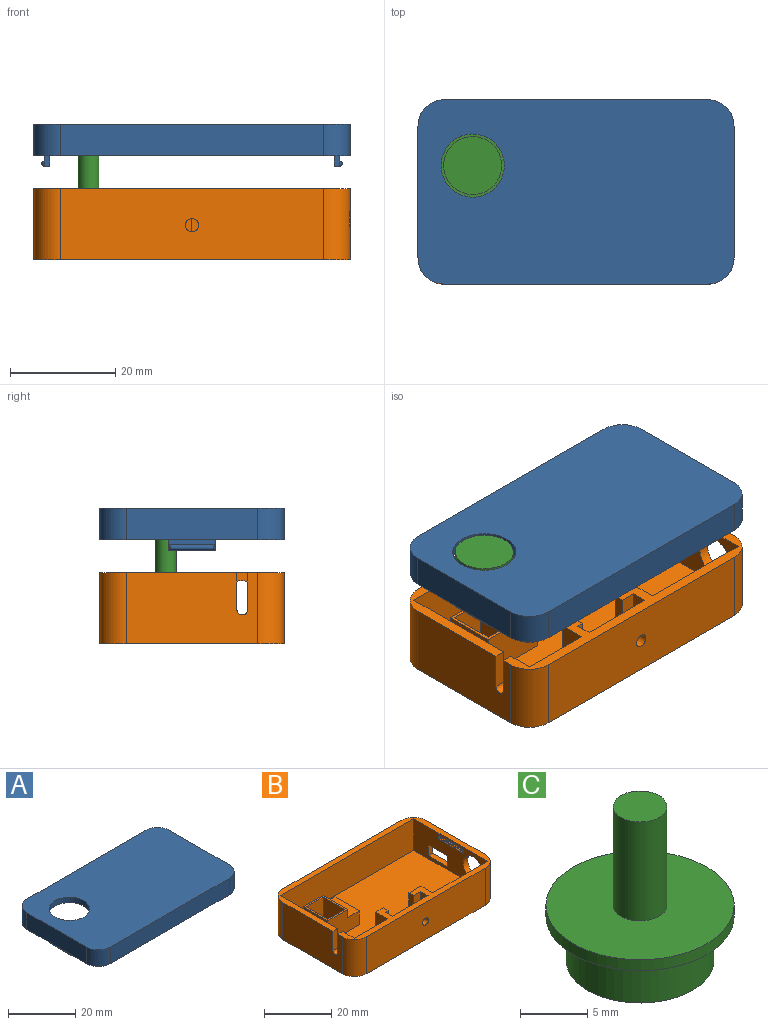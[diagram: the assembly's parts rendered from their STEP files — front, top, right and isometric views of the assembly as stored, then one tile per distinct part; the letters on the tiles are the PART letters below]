
ASSEMBLY  parts=3 mates=2
PART A: 30 faces, bbox 60x35x8 mm
  f0: plane 60x35mm, normal (0,0,-1), area 386.5mm2, adj f1,f2,f3,f4,f6,f7,f8,f9
  f1: plane 50x6mm, normal (0,1,0), area 300mm2, adj f0,f5,f28,f29
  f2: plane 25x6mm, normal (-1,0,0), area 150mm2, adj f0,f5,f26,f29
  f3: plane 50x6mm, normal (0,-1,0), area 300mm2, adj f0,f5,f26,f27
  f4: plane 25x6mm, normal (1,0,0), area 150mm2, adj f0,f5,f27,f28
  f5: plane 60x35mm, normal (0,0,1), area 1965.4mm2, adj f1,f2,f3,f4,f11,f26,f27,f28
  f6: plane 54x4mm, normal (0,-1,0), area 216mm2, adj f0,f7,f9,f10
  f7: plane 31x6mm, normal (1,0,0), area 142mm2, adj f0,f6,f8,f10,f12,f14,f15
  f8: plane 54x4mm, normal (0,1,0), area 216mm2, adj f0,f7,f9,f10
  f9: plane 31x6mm, normal (-1,0,0), area 142mm2, adj f0,f6,f8,f10,f17,f18,f19
  f10: plane 54x31mm, normal (0,0,-1), area 1560.9mm2, adj f6,f7,f8,f9,f11
  f11: cylinder r=6mm len=12mm, axis (0,0,-1), area 75.4mm2, adj f5,f10
  f12: plane 2x1mm, normal (0,1,0), area 2mm2, adj f0,f7,f13,f15,f22
  f13: plane 9x1mm, normal (-1,0,0), area 9mm2, adj f0,f12,f14,f21
  f14: plane 2x1mm, normal (0,-1,0), area 2mm2, adj f0,f7,f13,f15,f20
  f15: plane 9x1mm, normal (0,0,-1), area 9mm2, adj f7,f12,f14,f21
  f16: plane 9x1mm, normal (1,0,0), area 9mm2, adj f0,f17,f18,f23
  f17: plane 2x1mm, normal (0,1,0), area 2mm2, adj f0,f9,f16,f19,f24
  f18: plane 2x1mm, normal (0,-1,0), area 2mm2, adj f0,f9,f16,f19,f25
  f19: plane 9x1mm, normal (0,0,-1), area 9mm2, adj f9,f17,f18,f23
  f20: cylinder r=0.5mm len=1mm, axis (0,0,-1), area 0.5mm2, adj f14,f21
  f21: cylinder r=0.5mm len=9mm, axis (0,1,0), area 13.6mm2, adj f13,f15,f20,f22
  f22: cylinder r=0.5mm len=1mm, axis (0,0,1), area 0.5mm2, adj f12,f21
  f23: cylinder r=0.5mm len=9mm, axis (0,1,0), area 13.6mm2, adj f16,f19,f24,f25
  f24: cylinder r=0.5mm len=1mm, axis (0,0,1), area 0.5mm2, adj f17,f23
  f25: cylinder r=0.5mm len=1mm, axis (0,0,-1), area 0.5mm2, adj f18,f23
  f26: cylinder r=5mm len=6mm, axis (0,0,-1), area 47.1mm2, adj f0,f2,f3,f5
  f27: cylinder r=5mm len=6mm, axis (0,0,1), area 47.1mm2, adj f0,f3,f4,f5
  f28: cylinder r=5mm len=6mm, axis (0,0,-1), area 47.1mm2, adj f0,f1,f4,f5
  f29: cylinder r=5mm len=6mm, axis (0,0,1), area 47.1mm2, adj f0,f1,f2,f5
PART B: 74 faces, bbox 60x35x13.5 mm
  f0: plane 31x11.5mm, normal (1,0,0), area 324mm2, adj f2,f3,f7,f11,f54,f55,f56,f62
  f1: plane 25x13.5mm, normal (-1,0,0), area 321.9mm2, adj f7,f10,f54,f55,f56,f70,f71
  f2: plane 56x31mm, normal (0,0,1), area 1573mm2, adj f0,f3,f4,f5,f11,f12,f31,f32
  f3: plane 14x11.5mm, normal (0,1,0), area 161mm2, adj f0,f2,f7,f40
  f4: plane 15x11.5mm, normal (0,1,0), area 167.6mm2, adj f2,f7,f34,f36,f51
  f5: plane 31x11.5mm, normal (-1,0,0), area 250.8mm2, adj f2,f7,f11,f12,f13,f14,f15,f16
  f6: plane 25x13.5mm, normal (1,0,0), area 253.8mm2, adj f7,f10,f13,f14,f15,f16,f17,f72
  f7: plane 60x35mm, normal (0,0,1), area 366.9mm2, adj f0,f1,f3,f4,f5,f6,f8,f9
  f8: plane 50x13.5mm, normal (0,1,0), area 675mm2, adj f7,f10,f70,f73
  f9: plane 50x13.5mm, normal (0,-1,0), area 670.1mm2, adj f7,f10,f51,f71,f72
  f10: plane 60x35mm, normal (0,0,-1), area 2078.5mm2, adj f1,f6,f8,f9,f70,f71,f72,f73
  f11: plane 56x11.5mm, normal (0,-1,0), area 644mm2, adj f0,f2,f5,f7
  f12: plane 23x11.5mm, normal (0,1,0), area 264.5mm2, adj f2,f5,f7,f31
  f13: cylinder r=4.25mm len=8.5mm, axis (-1,0,0), area 52.9mm2, adj f5,f6,f72
  f14: plane 8x2mm, normal (0,0,-1), area 16mm2, adj f5,f6,f15,f17
  f15: plane 4x2mm, normal (0,-1,0), area 8mm2, adj f5,f6,f14,f16
  f16: plane 8x2mm, normal (0,0,1), area 16mm2, adj f5,f6,f15,f17
  f17: plane 4x2mm, normal (0,1,0), area 8mm2, adj f5,f6,f14,f16
  f18: plane 1x0.4mm, normal (0,-1,0), area 0.4mm2, adj f19,f21,f23,f27
  f19: plane 10x0.4mm, normal (0,0,1), area 4mm2, adj f18,f20,f24,f28
  f20: plane 1x0.4mm, normal (0,1,0), area 0.4mm2, adj f19,f21,f26,f30
  f21: plane 10x0.4mm, normal (0,0,-1), area 4mm2, adj f18,f20,f25,f29
  f22: plane 9.4x0.4mm, normal (-1,0,0), area 3.8mm2, adj f27,f28,f29,f30
  f23: cylinder r=0.3mm len=1.6mm, axis (0,0,-1), area 0.6mm2, adj f5,f18,f24,f25
  f24: cylinder r=0.3mm len=10.6mm, axis (0,-1,0), area 4.8mm2, adj f5,f19,f23,f26
  f25: cylinder r=0.3mm len=10.6mm, axis (0,1,0), area 4.8mm2, adj f5,f21,f23,f26
  f26: cylinder r=0.3mm len=1.6mm, axis (0,0,1), area 0.6mm2, adj f5,f20,f24,f25
  f27: cylinder r=0.3mm len=1mm, axis (0,0,-1), area 0.4mm2, adj f18,f22,f28,f29
  f28: cylinder r=0.3mm len=10mm, axis (0,-1,0), area 4.6mm2, adj f19,f22,f27,f30
  f29: cylinder r=0.3mm len=10mm, axis (0,1,0), area 4.6mm2, adj f21,f22,f27,f30
  f30: cylinder r=0.3mm len=1mm, axis (0,0,1), area 0.4mm2, adj f20,f22,f28,f29
  f31: plane 11.5x5mm, normal (1,0,0), area 57.5mm2, adj f2,f7,f12,f32
  f32: plane 11.5x5mm, normal (0,1,0), area 57.5mm2, adj f2,f7,f31,f33
  f33: plane 11.5x2mm, normal (-1,0,0), area 23mm2, adj f2,f7,f32,f35
  f34: plane 11.5x3mm, normal (-1,0,0), area 34.5mm2, adj f2,f4,f7,f35
  f35: plane 11.5x3mm, normal (0,-1,0), area 34.5mm2, adj f2,f7,f33,f34
  f36: plane 11.5x3mm, normal (1,0,0), area 34.5mm2, adj f2,f4,f7,f37
  f37: plane 11.5x1.2mm, normal (0,-1,0), area 13.8mm2, adj f2,f7,f36,f38
  f38: plane 11.5x2mm, normal (1,0,0), area 23mm2, adj f2,f7,f37,f39
  f39: plane 11.5x3.2mm, normal (0,1,0), area 36.8mm2, adj f2,f7,f38,f40
  f40: plane 11.5x5mm, normal (-1,0,0), area 57.5mm2, adj f2,f3,f7,f39
  f41: plane 10.2x8mm, normal (-1,0,0), area 81.6mm2, adj f2,f42,f48,f49
  f42: plane 13.2x8mm, normal (0,-1,0), area 90.6mm2, adj f2,f41,f43,f49,f52,f53
  f43: plane 10.2x3mm, normal (1,0,0), area 30.6mm2, adj f42,f48,f49,f52
  f44: plane 9x8mm, normal (-1,0,0), area 72mm2, adj f45,f47,f49,f50
  f45: plane 8x7mm, normal (0,1,0), area 56mm2, adj f44,f46,f49,f50
  f46: plane 9x8mm, normal (1,0,0), area 72mm2, adj f45,f47,f49,f50
  f47: plane 8x7mm, normal (0,-1,0), area 56mm2, adj f44,f46,f49,f50
  f48: plane 13.2x8mm, normal (0,1,0), area 90.6mm2, adj f2,f41,f43,f49,f52,f53
  f49: plane 10.2x8.2mm, normal (0,0,1), area 20.6mm2, adj f41,f42,f43,f44,f45,f46,f47,f48
  f50: plane 9x7mm, normal (0,0,1), area 63mm2, adj f44,f45,f46,f47
  f51: cylinder r=1.25mm len=2.5mm, axis (0,1,0), area 15.7mm2, adj f4,f9
  f52: plane 10.2x5mm, normal (0,0,1), area 51mm2, adj f42,f43,f48,f53
  f53: plane 10.2x5mm, normal (1,0,0), area 51mm2, adj f2,f42,f48,f52
  f54: plane 7x2mm, normal (0,1,0), area 14mm2, adj f0,f1,f7,f55
  f55: cylinder r=1mm len=2mm, axis (1,0,0), area 6.3mm2, adj f0,f1,f54,f56
  f56: plane 7x2mm, normal (0,-1,0), area 14mm2, adj f0,f1,f7,f55
  f57: plane 10x0.4mm, normal (0,0,1), area 4mm2, adj f58,f60,f62,f66
  f58: plane 1x0.4mm, normal (0,-1,0), area 0.4mm2, adj f57,f59,f63,f67
  f59: plane 10x0.4mm, normal (0,0,-1), area 4mm2, adj f58,f60,f65,f69
  f60: plane 1x0.4mm, normal (0,1,0), area 0.4mm2, adj f57,f59,f64,f68
  f61: plane 9.4x0.4mm, normal (1,0,0), area 3.8mm2, adj f66,f67,f68,f69
  f62: cylinder r=0.3mm len=10.6mm, axis (0,-1,0), area 4.8mm2, adj f0,f57,f63,f64
  f63: cylinder r=0.3mm len=1.6mm, axis (0,0,-1), area 0.6mm2, adj f0,f58,f62,f65
  f64: cylinder r=0.3mm len=1.6mm, axis (0,0,1), area 0.6mm2, adj f0,f60,f62,f65
  f65: cylinder r=0.3mm len=10.6mm, axis (0,1,0), area 4.8mm2, adj f0,f59,f63,f64
  f66: cylinder r=0.3mm len=10mm, axis (0,1,0), area 4.6mm2, adj f57,f61,f67,f68
  f67: cylinder r=0.3mm len=1mm, axis (0,0,1), area 0.4mm2, adj f58,f61,f66,f69
  f68: cylinder r=0.3mm len=1mm, axis (0,0,-1), area 0.4mm2, adj f60,f61,f66,f69
  f69: cylinder r=0.3mm len=10mm, axis (0,-1,0), area 4.6mm2, adj f59,f61,f67,f68
  f70: cylinder r=5mm len=13.5mm, axis (0,0,1), area 106mm2, adj f1,f7,f8,f10
  f71: cylinder r=5mm len=13.5mm, axis (0,0,-1), area 106mm2, adj f1,f7,f9,f10
  f72: cylinder r=5mm len=13.5mm, axis (0,0,1), area 100.9mm2, adj f6,f7,f9,f10,f13
  f73: cylinder r=5mm len=13.5mm, axis (0,0,-1), area 106mm2, adj f6,f7,f8,f10
PART C: 7 faces, bbox 14x14x14 mm
  f0: cylinder r=2mm len=9mm, axis (0,0,-1), area 113.1mm2, adj f1,f2
  f1: plane 4x4mm, normal (0,0,1), area 12.6mm2, adj f0
  f2: plane 14x14mm, normal (0,0,1), area 141.4mm2, adj f0,f3
  f3: cylinder r=7mm len=14mm, axis (0,0,1), area 44mm2, adj f2,f4
  f4: plane 14x14mm, normal (0,0,-1), area 58.9mm2, adj f3,f6
  f5: plane 11x11mm, normal (0,0,-1), area 95mm2, adj f6
  f6: cylinder r=5.5mm len=11mm, axis (0,0,1), area 138.2mm2, adj f4,f5
PLACE A t=(-1.53,0.2,4.29)mm
PLACE B t=(-1.53,0.2,-2)mm fixed
PLACE C rot(axis=(0,1,0),180deg) t=(-21.13,5.2,18.79)mm
MATE slider B.f7 <-> A.f0  axis (0,0,1) through (-26.53,-17.3,11.5)mm
MATE slider A.f11 <-> C.f6  axis (0,0,1) through (-21.13,5.2,23.79)mm
